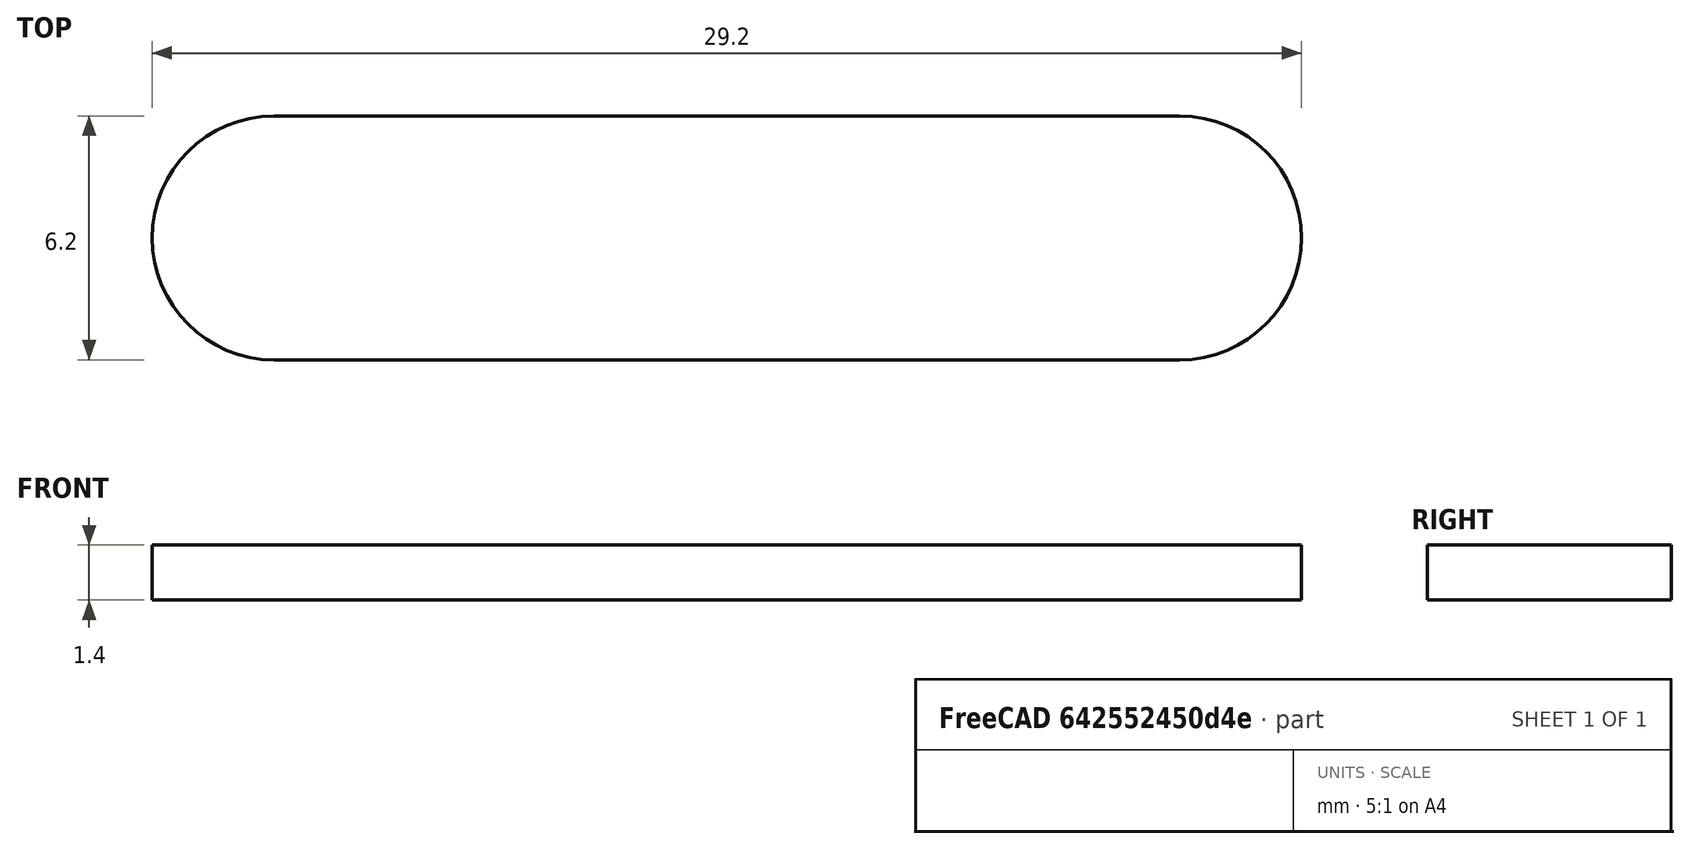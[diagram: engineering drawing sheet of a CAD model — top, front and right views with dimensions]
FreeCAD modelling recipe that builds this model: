
FCSTD DOCUMENT  (FreeCAD 1.0R39109 (Git))
Label: RK84_sticker
License: All rights reserved
LicenseURL: http://en.wikipedia.org/wiki/All_rights_reserved
objects: Sketcher::SketchObject×1, PartDesign::Pad×1, PartDesign::Body×1
note: 6 computed .brp shape members not serialized (recipe doc carries the construction recipe); baked Part::Feature solids carry a one-line shape summary decoded from their .brp

FEATURE [Sketcher::SketchObject] Sketch
  ArcFitTolerance = 0
  AttachmentSupport = -> [XY_Plane]
  FullyConstrained = true
  MakeInternals = false
  MapMode = 5
  sketch-geometry (7):
    g0: ArcOfCircle CenterX=-11.5 CenterY=0 CenterZ=0 NormalX=0 NormalY=0 NormalZ=1 AngleXU=0 Radius=3.1 StartAngle=1.5708 EndAngle=4.71239
    g1: ArcOfCircle CenterX=11.5 CenterY=0 CenterZ=0 NormalX=0 NormalY=0 NormalZ=1 AngleXU=0 Radius=3.1 StartAngle=4.71239 EndAngle=7.85398
    g2: LineSegment StartX=-11.5 StartY=-3.1 StartZ=0 EndX=11.5 EndY=-3.1 EndZ=0
    g3: LineSegment StartX=11.5 StartY=3.1 StartZ=0 EndX=-11.5 EndY=3.1 EndZ=0
    g4: GeomPoint [constr] X=-14.6 Y=0 Z=0
    g5: GeomPoint [constr] X=14.6 Y=0 Z=0
    g6: LineSegment [constr] StartX=-11.5 StartY=0 StartZ=0 EndX=11.5 EndY=0 EndZ=0
  constraints (15):
    c: Tangent(g0,g2) = -1.5708
    c: Tangent(g2,g1) = -1.5708
    c: Tangent(g1,g3) = -1.5708
    c: Tangent(g3,g0) = -1.5708
    c: Equal(g0,g1)
    c: Radius(g1) = 3.1
    c: PointOnObject(g4,g0)
    c: PointOnObject(g5,g1)
    c: Coincident(g6,g0)
    c: Coincident(g6,g1)
    c: PointOnObject(g5,g6)
    c: PointOnObject(g4,g6)
    c: DistanceX(g4,g5) = 29.2
    c: Symmetric(g0,g1,g-1)
    c: Horizontal(g6)
FEATURE [PartDesign::Pad] Pad
  Direction = (0,0,1)
  Length = 1.4
  Length2 = 10
  Profile = -> Sketch
  ReferenceAxis = -> Sketch [N_Axis]
  Suppressed = false
  Type = 0
FEATURE [PartDesign::Body] Body
  AllowCompound = false
  Group = -> [Sketch,Pad]
  Origin = -> Origin
  Tip = -> Pad
